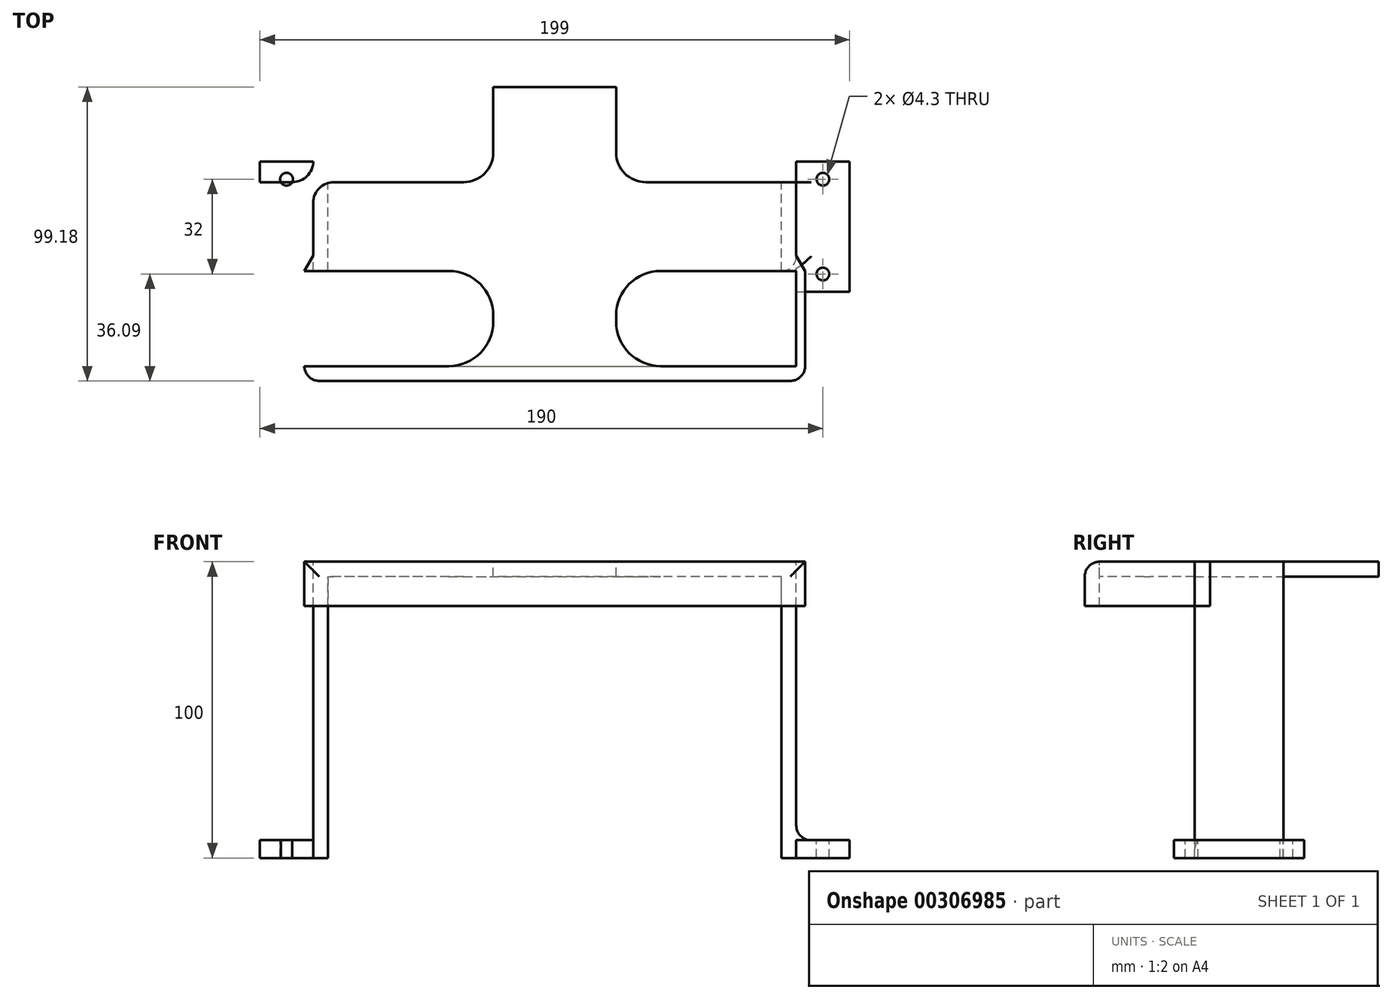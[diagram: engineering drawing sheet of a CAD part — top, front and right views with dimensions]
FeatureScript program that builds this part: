
annotation { "Feature Type Name" : "Feature", "Feature Type Description" : "" }
export const myFeature = defineFeature(function(context is Context, id is Id, definition is map)
    precondition{}
    {
        {
            var Q0;
            Q0=qCreatedBy(makeId("Front.planeOp"),FACE);
            var sketch = newSketch(context, id + "F0", { "sketchPlane" : qUnion([Q0])});
            skLineSegment(sketch, "E0.bottom", {"start": v(76.5, -47.5) * mm, "end": v(-76.5, -47.5) * mm});
            skLineSegment(sketch, "E0.top", {"start": v(76.5, 47.5) * mm, "end": v(-76.5, 47.5) * mm});
            skLineSegment(sketch, "E0.left", {"start": v(76.5, -47.5) * mm, "end": v(76.5, 47.5) * mm});
            skLineSegment(sketch, "E0.right", {"start": v(-76.5, -47.5) * mm, "end": v(-76.5, 47.5) * mm});
            skPoint(sketch, "E0.middle", {"position": v(0, 0) * mm});
            skLineSegment(sketch, "E1", {"start": v(-76.5, -47.5) * mm, "end": v(-99.5, -47.5) * mm});
            skLineSegment(sketch, "E2", {"start": v(-99.5, -47.5) * mm, "end": v(-99.5, -41.5) * mm});
            skLineSegment(sketch, "E3", {"start": v(-99.5, -41.5) * mm, "end": v(99.5, -41.5) * mm});
            skLineSegment(sketch, "E4", {"start": v(99.5, -41.5) * mm, "end": v(99.5, -47.5) * mm});
            skLineSegment(sketch, "E5", {"start": v(99.5, -47.5) * mm, "end": v(76.5, -47.5) * mm});
            skLineSegment(sketch, "E6.bottom", {"start": v(-81.5, -41.5) * mm, "end": v(81.5, -41.5) * mm});
            skLineSegment(sketch, "E6.top", {"start": v(-81.5, 52.5) * mm, "end": v(81.5, 52.5) * mm});
            skLineSegment(sketch, "E6.left", {"start": v(-81.5, -41.5) * mm, "end": v(-81.5, 52.5) * mm});
            skLineSegment(sketch, "E6.right", {"start": v(81.5, -41.5) * mm, "end": v(81.5, 52.5) * mm});
            skSolve(sketch);
        }
        {
            var Q0;
            {var subQ5=sQuery(id+"F0.wireOp",EDGE,"E0.top");Q0=makeQuery(id+"F0.imprint","IMPRINT",FACE,{"disambiguationData":[TD([[makeQuery(id+"F0.imprint","IMPRINT",EDGE,{"derivedFrom":subQ5}),-1.0]])]});}
            var Q1;
            {var subQ4=sQuery(id+"F0.wireOp",EDGE,"E1");Q1=makeQuery(id+"F0.imprint","IMPRINT",FACE,{"disambiguationData":[TD([[makeQuery(id+"F0.imprint","IMPRINT",EDGE,{"derivedFrom":subQ4}),-1.0]])]});}
            var Q2;
            {var subQ1=sQuery(id+"F0.wireOp",EDGE,"E4");Q2=makeQuery(id+"F0.imprint","IMPRINT",FACE,{"disambiguationData":[TD([[makeQuery(id+"F0.imprint","IMPRINT",EDGE,{"derivedFrom":subQ1}),-1.0]])]});}
            extrude(context, id + "F1", {"entities" : qUnion([Q0, Q1, Q2]), "depth" : 30 * mm});
        }
        {
            var Q0;
            {var subQ0=sQuery(id+"F0.wireOp",EDGE,"E3");Q0=makeQuery(id+"F1.opExtrude","SWEPT_FACE",FACE,{"disambiguationData":[OSD([subQ0]),TDD([makeQuery(id+"F0.imprint","IMPRINT",EDGE,{"disambiguationData":[TD([[makeQuery(id+"F0.imprint","INTERSECT",VERTEX,{"derivedFrom":[subQ0,sQuery(id+"F0.wireOp",EDGE,"E4")]}),1.0]])],"derivedFrom":subQ0})])]});}
            var sketch = newSketch(context, id + "F2", { "sketchPlane" : qUnion([Q0])});
            skLineSegment(sketch, "E7", {"start": v(90.5, 0) * mm, "end": v(90.5, -30) * mm, "construction": true});
            skLineSegment(sketch, "E8", {"start": v(81.5, 1) * mm, "end": v(99.5, 1) * mm, "construction": true});
            skLineSegment(sketch, "E9", {"start": v(99.5, -31) * mm, "end": v(81.5, -31) * mm, "construction": true});
            skCircle(sketch, "E10", {"center": v(90.5, 1) * mm, "radius": 2.15 * mm});
            skCircle(sketch, "E11", {"center": v(90.5, -31) * mm, "radius": 2.15 * mm});
            skLineSegment(sketch, "E12", {"start": v(-81.5, 0) * mm, "end": v(-99.5, 0) * mm, "construction": true});
            skLineSegment(sketch, "E13.bottom", {"start": v(-99.5, 0) * mm, "end": v(-81.5, 0) * mm});
            skLineSegment(sketch, "E13.top", {"start": v(-99.5, -30) * mm, "end": v(-81.5, -30) * mm, "construction": true});
            skLineSegment(sketch, "E13.left", {"start": v(-99.5, 0) * mm, "end": v(-99.5, -30) * mm, "construction": true});
            skLineSegment(sketch, "E13.right", {"start": v(-81.5, 0) * mm, "end": v(-81.5, -30) * mm, "construction": true});
            skLineSegment(sketch, "E14", {"start": v(-99.5, 1) * mm, "end": v(-81.5, 1) * mm, "construction": true});
            skLineSegment(sketch, "E15", {"start": v(-81.5, 1) * mm, "end": v(-81.5, -31) * mm, "construction": true});
            skLineSegment(sketch, "E16", {"start": v(-81.5, -31) * mm, "end": v(-99.5, -31) * mm, "construction": true});
            skCircle(sketch, "E17", {"center": v(-90.5, 1) * mm, "radius": 2.15 * mm});
            skCircle(sketch, "E18", {"center": v(-90.5, -31) * mm, "radius": 2.15 * mm});
            skLineSegment(sketch, "E19.bottom", {"start": v(81.5, -37) * mm, "end": v(99.5, -37) * mm});
            skLineSegment(sketch, "E19.top", {"start": v(81.5, 7) * mm, "end": v(99.5, 7) * mm});
            skLineSegment(sketch, "E19.left", {"start": v(81.5, -37) * mm, "end": v(81.5, 7) * mm});
            skLineSegment(sketch, "E19.right", {"start": v(99.5, -37) * mm, "end": v(99.5, 7) * mm});
            skLineSegment(sketch, "E20.bottom", {"start": v(-99.5, -37) * mm, "end": v(-81.5, -37) * mm});
            skLineSegment(sketch, "E20.top", {"start": v(-99.5, 7) * mm, "end": v(-81.5, 7) * mm});
            skLineSegment(sketch, "E20.left", {"start": v(-99.5, -37) * mm, "end": v(-99.5, 7) * mm});
            skLineSegment(sketch, "E20.right", {"start": v(-81.5, -37) * mm, "end": v(-81.5, 7) * mm});
            skSolve(sketch);
        }
        {
            var Q0;
            Q0=makeQuery(id+"F1.opExtrude","SWEPT_FACE",FACE,{"disambiguationData":[OSD([sQuery(id+"F0.wireOp",EDGE,"E6.top")])]});
            var sketch = newSketch(context, id + "F3", { "sketchPlane" : qUnion([Q0])});
            skLineSegment(sketch, "E21.bottom", {"start": v(30.72, 0) * mm, "end": v(81.5, 0) * mm});
            skLineSegment(sketch, "E21.top", {"start": v(-81.5, -30) * mm, "end": v(-35.72, -30) * mm});
            skLineSegment(sketch, "E21.left", {"start": v(-81.5, 0) * mm, "end": v(-81.5, -30) * mm});
            skLineSegment(sketch, "E21.right", {"start": v(81.5, 0) * mm, "end": v(81.5, -30) * mm});
            skLineSegment(sketch, "E22", {"start": v(0, 0) * mm, "end": v(0, -30) * mm, "construction": true});
            skLineSegment(sketch, "E23.top", {"start": v(20.72, 32.1) * mm, "end": v(-20.72, 32.1) * mm});
            skLineSegment(sketch, "E23.left", {"start": v(20.72, -47.09) * mm, "end": v(20.72, -45) * mm});
            skLineSegment(sketch, "E23.right", {"start": v(-20.72, -47.1) * mm, "end": v(-20.72, -45) * mm});
            skPoint(sketch, "E23.middle", {"position": v(0, -15) * mm});
            skLineSegment(sketch, "E24.bottom", {"start": v(-81.5, -62.09) * mm, "end": v(-35.72, -62.09) * mm});
            skLineSegment(sketch, "E24.top", {"start": v(-81.5, -67.1) * mm, "end": v(81.5, -67.1) * mm});
            skLineSegment(sketch, "E24.left", {"start": v(-81.5, -62.09) * mm, "end": v(-81.5, -67.1) * mm});
            skLineSegment(sketch, "E24.right", {"start": v(81.5, -62.09) * mm, "end": v(81.5, -67.09) * mm});
            skLineSegment(sketch, "E25.bottom", {"start": v(81.5, -62.09) * mm, "end": v(84.5, -62.09) * mm});
            skLineSegment(sketch, "E25.top", {"start": v(81.5, -67.1) * mm, "end": v(84.5, -67.1) * mm});
            skLineSegment(sketch, "E25.left", {"start": v(81.5, -62.09) * mm, "end": v(81.5, -67.1) * mm});
            skLineSegment(sketch, "E25.right", {"start": v(84.5, -62.09) * mm, "end": v(84.5, -67.09) * mm});
            skLineSegment(sketch, "E26.bottom", {"start": v(-81.5, -67.1) * mm, "end": v(-84.5, -67.1) * mm});
            skLineSegment(sketch, "E26.top", {"start": v(-81.5, -62.09) * mm, "end": v(-84.5, -62.09) * mm});
            skLineSegment(sketch, "E26.left", {"start": v(-81.5, -67.1) * mm, "end": v(-81.5, -62.09) * mm});
            skLineSegment(sketch, "E26.right", {"start": v(-84.5, -67.1) * mm, "end": v(-84.5, -62.09) * mm});
            skLineSegment(sketch, "E27.trimOffspring", {"start": v(35.72, -62.09) * mm, "end": v(81.5, -62.09) * mm});
            skPoint(sketch, "E28.visualSharp", {"position": v(20.72, -62.09) * mm});
            skArc(sketch, "E28.filletArc", {"start": v(20.72, -47.1) * mm, "mid": v(25.12, -57.7) * mm, "end": v(35.72, -62.09) * mm});
            skPoint(sketch, "E29.visualSharp", {"position": v(-20.72, -62.09) * mm});
            skArc(sketch, "E29.filletArc", {"start": v(-35.72, -62.1) * mm, "mid": v(-25.12, -57.7) * mm, "end": v(-20.72, -47.1) * mm});
            skLineSegment(sketch, "E30", {"start": v(20.72, 10) * mm, "end": v(20.72, 32.1) * mm});
            skLineSegment(sketch, "E31", {"start": v(35.72, -30) * mm, "end": v(81.5, -30) * mm});
            skArc(sketch, "E32.filletArc", {"start": v(-20.72, -45) * mm, "mid": v(-25.12, -34.4) * mm, "end": v(-35.72, -30) * mm});
            skArc(sketch, "E33.filletArc", {"start": v(35.72, -30) * mm, "mid": v(25.12, -34.4) * mm, "end": v(20.72, -45) * mm});
            skLineSegment(sketch, "E34", {"start": v(-20.72, 32.1) * mm, "end": v(-20.72, 10) * mm});
            skLineSegment(sketch, "E35.bottom", {"start": v(-20.72, 32.1) * mm, "end": v(20.72, 32.1) * mm});
            skLineSegment(sketch, "E35.top", {"start": v(-20.72, 37.09) * mm, "end": v(20.72, 37.09) * mm});
            skLineSegment(sketch, "E35.left", {"start": v(-20.72, 32.1) * mm, "end": v(-20.72, 37.09) * mm});
            skLineSegment(sketch, "E35.right", {"start": v(20.72, 32.1) * mm, "end": v(20.72, 37.09) * mm});
            skArc(sketch, "E36.filletArc", {"start": v(20.72, 10) * mm, "mid": v(23.65, 2.93) * mm, "end": v(30.72, 0) * mm});
            skLineSegment(sketch, "E37", {"start": v(-30.72, 0) * mm, "end": v(-32.78, 0) * mm});
            skPoint(sketch, "E38.visualSharp", {"position": v(-20.72, 0) * mm});
            skArc(sketch, "E38.filletArc", {"start": v(-30.72, 0) * mm, "mid": v(-23.65, 2.93) * mm, "end": v(-20.72, 10) * mm});
            skLineSegment(sketch, "E39", {"start": v(-81.5, -62.09) * mm, "end": v(81.5, -62.09) * mm});
            skLineSegment(sketch, "E40", {"start": v(30.72, 0) * mm, "end": v(-30.72, 0) * mm});
            skLineSegment(sketch, "E41.bottom", {"start": v(-84.5, -62.09) * mm, "end": v(-81.5, -62.09) * mm});
            skLineSegment(sketch, "E41.top", {"start": v(-84.5, -30) * mm, "end": v(-81.5, -30) * mm});
            skLineSegment(sketch, "E41.left", {"start": v(-84.5, -62.09) * mm, "end": v(-84.5, -30) * mm});
            skLineSegment(sketch, "E41.right", {"start": v(-81.5, -62.09) * mm, "end": v(-81.5, -30) * mm});
            skLineSegment(sketch, "E42.top", {"start": v(81.5, -30) * mm, "end": v(84.5, -30) * mm});
            skLineSegment(sketch, "E42.left", {"start": v(81.5, -62.09) * mm, "end": v(81.5, -30) * mm});
            skLineSegment(sketch, "E42.right", {"start": v(84.5, -62.09) * mm, "end": v(84.5, -30) * mm});
            skLineSegment(sketch, "E43", {"start": v(-84.5, -30) * mm, "end": v(-81.5, -24.8) * mm});
            skLineSegment(sketch, "E44", {"start": v(84.5, -30) * mm, "end": v(81.5, -24.8) * mm});
            skSolve(sketch);
        }
        {
            var Q0;
            Q0=makeQuery(id+"F3.imprint","IMPRINT",FACE,{"disambiguationData":[TD([[makeQuery(id+"F3.imprint","IMPRINT",EDGE,{"derivedFrom":sQuery(id+"F3.wireOp",EDGE,"E30")}),1.0]])]});
            var Q1;
            Q1=makeQuery(id+"F3.imprint","IMPRINT",FACE,{"disambiguationData":[TD([[makeQuery(id+"F3.imprint","IMPRINT",EDGE,{"derivedFrom":sQuery(id+"F3.wireOp",EDGE,"E23.left")}),1.0]])]});
            extrude(context, id + "F4", {"entities" : qUnion([Q0, Q1]), "operationType" : NewBodyOperationType.ADD, "oppositeDirection" : true, "depth" : 5 * mm});
        }
        {
            var Q0;
            Q0=makeQuery(id+"F3.imprint","IMPRINT",FACE,{"disambiguationData":[TD([[makeQuery(id+"F3.imprint","IMPRINT",EDGE,{"derivedFrom":sQuery(id+"F3.wireOp",EDGE,"E41.bottom")}),1.0]])]});
            var Q1;
            Q1=makeQuery(id+"F3.imprint","IMPRINT",FACE,{"disambiguationData":[TD([[makeQuery(id+"F3.imprint","IMPRINT",EDGE,{"derivedFrom":sQuery(id+"F3.wireOp",EDGE,"E24.top")}),1.0]])]});
            var Q2;
            Q2=makeQuery(id+"F3.imprint","IMPRINT",FACE,{"disambiguationData":[TD([[makeQuery(id+"F3.imprint","IMPRINT",EDGE,{"derivedFrom":sQuery(id+"F3.wireOp",EDGE,"E26.bottom")}),-1.0]])]});
            var Q3;
            Q3=makeQuery(id+"F3.imprint","IMPRINT",FACE,{"disambiguationData":[TD([[makeQuery(id+"F3.imprint","IMPRINT",EDGE,{"derivedFrom":sQuery(id+"F3.wireOp",EDGE,"E25.bottom")}),1.0]])]});
            var Q4;
            Q4=makeQuery(id+"F3.imprint","IMPRINT",FACE,{"disambiguationData":[TD([[makeQuery(id+"F3.imprint","IMPRINT",EDGE,{"derivedFrom":sQuery(id+"F3.wireOp",EDGE,"E25.top")}),1.0]])]});
            var Q5;
            {var subQ0=sQuery(id+"F3.wireOp",EDGE,"E42.top");Q5=makeQuery(id+"F3.imprint","IMPRINT",FACE,{"disambiguationData":[TD([[makeQuery(id+"F3.imprint","IMPRINT",EDGE,{"derivedFrom":subQ0}),1.0]])]});}
            var Q6;
            {var subQ0=sQuery(id+"F3.wireOp",EDGE,"E41.top");Q6=makeQuery(id+"F3.imprint","IMPRINT",FACE,{"disambiguationData":[TD([[makeQuery(id+"F3.imprint","IMPRINT",EDGE,{"derivedFrom":subQ0}),1.0]])]});}
            var Q7;
            Q7=makeQuery(id+"F3.imprint","IMPRINT",FACE,{"disambiguationData":[TD([[makeQuery(id+"F3.imprint","IMPRINT",EDGE,{"derivedFrom":sQuery(id+"F3.wireOp",EDGE,"E35.bottom")}),1.0]])]});
            extrude(context, id + "F5", {"entities" : qUnion([Q0, Q1, Q2, Q3, Q4, Q5, Q6, Q7]), "operationType" : NewBodyOperationType.ADD, "oppositeDirection" : true, "depth" : 15 * mm});
        }
        {
            var Q0;
            Q0=makeQuery(id+"F5.opExtrude","SWEPT_EDGE",EDGE,{"disambiguationData":[OSD([sQuery(id+"F3.wireOp",EDGE,"E25.top"),sQuery(id+"F3.wireOp",EDGE,"E25.right")])]});
            var Q1;
            Q1=makeQuery(id+"F5.opExtrude","SWEPT_EDGE",EDGE,{"disambiguationData":[OSD([sQuery(id+"F3.wireOp",EDGE,"E26.bottom"),sQuery(id+"F3.wireOp",EDGE,"E26.right")])]});
            var Q2;
            Q2=makeQuery(id+"F5.opExtrude","CAP_EDGE",EDGE,{"disambiguationData":[OSD([sQuery(id+"F3.wireOp",EDGE,"E24.top"),sQuery(id+"F3.wireOp",EDGE,"E25.top"),sQuery(id+"F3.wireOp",EDGE,"E26.bottom")])],"isStart":true});
            fillet(context, id + "F6", {"entities" : qUnion([Q0, Q1, Q2]), "radius" : 5 * mm, "tangentPropagation" : true, "allowEdgeOverflow" : false});
        }
        {
            var Q0;
            {var subQ4=sQuery(id+"F2.wireOp",EDGE,"E19.top");Q0=makeQuery(id+"F2.imprint","IMPRINT",FACE,{"disambiguationData":[TD([[makeQuery(id+"F2.imprint","IMPRINT",EDGE,{"derivedFrom":subQ4}),-1.0]])]});}
            var Q1;
            {var subQ4=sQuery(id+"F2.wireOp",EDGE,"E19.bottom");Q1=makeQuery(id+"F2.imprint","IMPRINT",FACE,{"disambiguationData":[TD([[makeQuery(id+"F2.imprint","IMPRINT",EDGE,{"derivedFrom":subQ4}),1.0]])]});}
            var Q2;
            Q2=makeQuery(id+"F2.imprint","IMPRINT",FACE,{"disambiguationData":[TD([[makeQuery(id+"F2.imprint","IMPRINT",EDGE,{"derivedFrom":sQuery(id+"F2.wireOp",EDGE,"E18")}),-1.0]])]});
            var Q3;
            {var subQ4=sQuery(id+"F2.wireOp",EDGE,"E20.top");Q3=makeQuery(id+"F2.imprint","IMPRINT",FACE,{"disambiguationData":[TD([[makeQuery(id+"F2.imprint","IMPRINT",EDGE,{"derivedFrom":subQ4}),-1.0]])]});}
            extrude(context, id + "F7", {"entities" : qUnion([Q0, Q1, Q2, Q3]), "operationType" : NewBodyOperationType.ADD, "oppositeDirection" : true, "depth" : 6 * mm});
        }
        {
            var Q0;
            {var subQ0=sQuery(id+"F2.wireOp",EDGE,"E11");var subQ1=sQuery(id+"F0.wireOp",EDGE,"E3");var subQ2=makeQuery(id+"F1.opExtrude","CAP_EDGE",EDGE,{"disambiguationData":[OSD([subQ1]),TDD([makeQuery(id+"F0.imprint","IMPRINT",EDGE,{"disambiguationData":[TD([[makeQuery(id+"F0.imprint","INTERSECT",VERTEX,{"derivedFrom":[subQ1,sQuery(id+"F0.wireOp",EDGE,"E4")]}),1.0]])],"derivedFrom":subQ1})])],"isStart":false});var subQ3=makeQuery(id+"F2.imprint","INTERSECT",VERTEX,{"disambiguationData":[OD(0.0)],"derivedFrom":[subQ2,subQ0]});Q0=makeQuery(id+"F2.imprint","IMPRINT",FACE,{"disambiguationData":[TD([[makeQuery(id+"F2.imprint","IMPRINT",EDGE,{"disambiguationData":[TD([[subQ3,-1.0]])],"derivedFrom":subQ0}),1.0]])]});}
            var Q1;
            {var subQ0=sQuery(id+"F2.wireOp",EDGE,"E10");var subQ1=sQuery(id+"F0.wireOp",EDGE,"E3");var subQ2=makeQuery(id+"F1.opExtrude","CAP_EDGE",EDGE,{"disambiguationData":[OSD([subQ1]),TDD([makeQuery(id+"F0.imprint","IMPRINT",EDGE,{"disambiguationData":[TD([[makeQuery(id+"F0.imprint","INTERSECT",VERTEX,{"derivedFrom":[subQ1,sQuery(id+"F0.wireOp",EDGE,"E4")]}),1.0]])],"derivedFrom":subQ1})])],"isStart":true});var subQ3=makeQuery(id+"F2.imprint","INTERSECT",VERTEX,{"disambiguationData":[OD(0.0)],"derivedFrom":[subQ2,subQ0]});Q1=makeQuery(id+"F2.imprint","IMPRINT",FACE,{"disambiguationData":[TD([[makeQuery(id+"F2.imprint","IMPRINT",EDGE,{"disambiguationData":[TD([[subQ3,1.0]])],"derivedFrom":subQ0}),1.0]])]});}
            var Q2;
            Q2=makeQuery(id+"F2.imprint","IMPRINT",FACE,{"disambiguationData":[TD([[makeQuery(id+"F2.imprint","IMPRINT",EDGE,{"derivedFrom":sQuery(id+"F2.wireOp",EDGE,"E18")}),1.0]])]});
            var Q3;
            {var subQ0=sQuery(id+"F2.wireOp",EDGE,"E17");var subQ1=sQuery(id+"F2.wireOp",EDGE,"E13.bottom");var subQ2=makeQuery(id+"F2.imprint","INTERSECT",VERTEX,{"disambiguationData":[OD(0.0)],"derivedFrom":[subQ1,subQ0]});Q3=makeQuery(id+"F2.imprint","IMPRINT",FACE,{"disambiguationData":[TD([[makeQuery(id+"F2.imprint","IMPRINT",EDGE,{"disambiguationData":[TD([[subQ2,-1.0]])],"derivedFrom":subQ1}),-1.0]])]});}
            extrude(context, id + "F8", {"entities" : qUnion([Q0, Q1, Q2, Q3]), "operationType" : NewBodyOperationType.REMOVE, "oppositeDirection" : true, "depth" : 25 * mm});
        }
        {
            var Q0;
            {var subQ0=sQuery(id+"F2.wireOp",EDGE,"E19.left");var subQ1=sQuery(id+"F0.wireOp",EDGE,"E3");Q0=makeQuery(id+"F7.opExtrude","SWEPT_EDGE",EDGE,{"disambiguationData":[OSD([subQ1,subQ0]),TDD([makeQuery(id+"F2.imprint","INTERSECT",VERTEX,{"derivedFrom":[makeQuery(id+"F1.opExtrude","CAP_EDGE",EDGE,{"disambiguationData":[OSD([subQ1]),TDD([makeQuery(id+"F0.imprint","IMPRINT",EDGE,{"disambiguationData":[TD([[makeQuery(id+"F0.imprint","INTERSECT",VERTEX,{"derivedFrom":[subQ1,sQuery(id+"F0.wireOp",EDGE,"E4")]}),1.0]])],"derivedFrom":subQ1})])],"isStart":false}),subQ0]})])]});}
            var Q1;
            {var subQ0=sQuery(id+"F2.wireOp",EDGE,"E19.left");var subQ1=sQuery(id+"F0.wireOp",EDGE,"E3");Q1=makeQuery(id+"F7.opExtrude","SWEPT_EDGE",EDGE,{"disambiguationData":[OSD([subQ1,subQ0]),TDD([makeQuery(id+"F2.imprint","INTERSECT",VERTEX,{"derivedFrom":[makeQuery(id+"F1.opExtrude","CAP_EDGE",EDGE,{"disambiguationData":[OSD([subQ1]),TDD([makeQuery(id+"F0.imprint","IMPRINT",EDGE,{"disambiguationData":[TD([[makeQuery(id+"F0.imprint","INTERSECT",VERTEX,{"derivedFrom":[subQ1,sQuery(id+"F0.wireOp",EDGE,"E4")]}),1.0]])],"derivedFrom":subQ1})])],"isStart":true}),subQ0]})])]});}
            var Q2;
            {var subQ7=sQuery(id+"F0.wireOp",EDGE,"E6.top");var subQ8=sQuery(id+"F0.wireOp",EDGE,"E0.top");var subQ9=sQuery(id+"F0.wireOp",EDGE,"E6.left");var subQ10=sQuery(id+"F0.wireOp",EDGE,"E3");var subQ11=sQuery(id+"F0.wireOp",EDGE,"E2");var subQ18=sQuery(id+"F0.wireOp",EDGE,"E1");var subQ19=sQuery(id+"F0.wireOp",EDGE,"E0.right");Q2=makeQuery(id+"F7.boolean.opBoolean","INTERSECT",EDGE,{"derivedFrom":[makeQuery(id+"F4.boolean.opBoolean","SPLIT",FACE,{"disambiguationData":[TD([makeQuery(id+"F1.opExtrude","SWEPT_FACE",FACE,{"disambiguationData":[OSD([subQ19])]})])],"derivedFrom":makeQuery(id+"F1.opExtrude","CAP_FACE",FACE,{"disambiguationData":[OSD([subQ8,sQuery(id+"F0.wireOp",EDGE,"E0.left"),subQ19,subQ18,subQ11,subQ10,sQuery(id+"F0.wireOp",EDGE,"E4"),sQuery(id+"F0.wireOp",EDGE,"E5"),subQ7,subQ9,sQuery(id+"F0.wireOp",EDGE,"E6.right")])],"isStart":true})}),makeQuery(id+"F7.opExtrude","SWEPT_FACE",FACE,{"disambiguationData":[OSD([sQuery(id+"F2.wireOp",EDGE,"E20.right")])]})]});}
            var Q3;
            {var subQ7=sQuery(id+"F0.wireOp",EDGE,"E6.top");var subQ8=sQuery(id+"F0.wireOp",EDGE,"E0.top");var subQ9=sQuery(id+"F0.wireOp",EDGE,"E6.left");var subQ10=sQuery(id+"F0.wireOp",EDGE,"E3");var subQ11=sQuery(id+"F0.wireOp",EDGE,"E2");var subQ18=sQuery(id+"F0.wireOp",EDGE,"E1");var subQ19=sQuery(id+"F0.wireOp",EDGE,"E0.right");Q3=makeQuery(id+"F7.boolean.opBoolean","INTERSECT",EDGE,{"derivedFrom":[makeQuery(id+"F4.boolean.opBoolean","SPLIT",FACE,{"disambiguationData":[TD([makeQuery(id+"F1.opExtrude","SWEPT_FACE",FACE,{"disambiguationData":[OSD([subQ19])]})])],"derivedFrom":makeQuery(id+"F1.opExtrude","CAP_FACE",FACE,{"disambiguationData":[OSD([subQ8,sQuery(id+"F0.wireOp",EDGE,"E0.left"),subQ19,subQ18,subQ11,subQ10,sQuery(id+"F0.wireOp",EDGE,"E4"),sQuery(id+"F0.wireOp",EDGE,"E5"),subQ7,subQ9,sQuery(id+"F0.wireOp",EDGE,"E6.right")])],"isStart":false})}),makeQuery(id+"F7.opExtrude","SWEPT_FACE",FACE,{"disambiguationData":[OSD([sQuery(id+"F2.wireOp",EDGE,"E20.right")])]})]});}
            fillet(context, id + "F9", {"entities" : qUnion([Q0, Q1, Q2, Q3]), "radius" : 7 * mm, "tangentPropagation" : true, "allowEdgeOverflow" : false});
        }
        {
            var Q0;
            Q0=makeQuery(id+"F9.opFillet","TWEAK_EDGE",EDGE,{"derivedFrom":[makeQuery(id+"F1.opExtrude","CAP_VERTEX",VERTEX,{"disambiguationData":[OSD([sQuery(id+"F0.wireOp",EDGE,"E3"),sQuery(id+"F0.wireOp",EDGE,"E6.bottom"),sQuery(id+"F0.wireOp",EDGE,"E6.left")])],"isStart":false})]});
            var Q1;
            Q1=makeQuery(id+"F9.opFillet","TWEAK_EDGE",EDGE,{"derivedFrom":[makeQuery(id+"F1.opExtrude","CAP_VERTEX",VERTEX,{"disambiguationData":[OSD([sQuery(id+"F0.wireOp",EDGE,"E3"),sQuery(id+"F0.wireOp",EDGE,"E6.bottom"),sQuery(id+"F0.wireOp",EDGE,"E6.left")])],"isStart":true})]});
            var Q2;
            {var subQ0=sQuery(id+"F2.wireOp",EDGE,"E19.left");var subQ1=sQuery(id+"F0.wireOp",EDGE,"E3");var subQ2=sQuery(id+"F0.wireOp",EDGE,"E6.right");var subQ3=sQuery(id+"F0.wireOp",EDGE,"E6.bottom");Q2=makeQuery(id+"F9.opFillet","TWEAK_EDGE",EDGE,{"derivedFrom":[makeQuery(id+"F7.boolean.opBoolean","MERGE",VERTEX,{"derivedFrom":[makeQuery(id+"F1.opExtrude","CAP_VERTEX",VERTEX,{"disambiguationData":[OSD([subQ1,subQ3,subQ2])],"isStart":true}),makeQuery(id+"F7.opExtrude","CAP_VERTEX",VERTEX,{"disambiguationData":[OSD([subQ1,subQ0]),TDD([makeQuery(id+"F2.imprint","INTERSECT",VERTEX,{"derivedFrom":[makeQuery(id+"F1.opExtrude","CAP_EDGE",EDGE,{"disambiguationData":[OSD([subQ1]),TDD([makeQuery(id+"F0.imprint","IMPRINT",EDGE,{"disambiguationData":[TD([[makeQuery(id+"F0.imprint","INTERSECT",VERTEX,{"derivedFrom":[subQ1,sQuery(id+"F0.wireOp",EDGE,"E4")]}),1.0]])],"derivedFrom":subQ1})])],"isStart":true}),subQ0]})])],"isStart":true})]})]});}
            var Q3;
            {var subQ0=sQuery(id+"F2.wireOp",EDGE,"E19.left");var subQ1=sQuery(id+"F0.wireOp",EDGE,"E3");var subQ2=sQuery(id+"F0.wireOp",EDGE,"E6.right");var subQ3=sQuery(id+"F0.wireOp",EDGE,"E6.bottom");Q3=makeQuery(id+"F9.opFillet","TWEAK_EDGE",EDGE,{"derivedFrom":[makeQuery(id+"F7.boolean.opBoolean","MERGE",VERTEX,{"derivedFrom":[makeQuery(id+"F1.opExtrude","CAP_VERTEX",VERTEX,{"disambiguationData":[OSD([subQ1,subQ3,subQ2])],"isStart":false}),makeQuery(id+"F7.opExtrude","CAP_VERTEX",VERTEX,{"disambiguationData":[OSD([subQ1,subQ0]),TDD([makeQuery(id+"F2.imprint","INTERSECT",VERTEX,{"derivedFrom":[makeQuery(id+"F1.opExtrude","CAP_EDGE",EDGE,{"disambiguationData":[OSD([subQ1]),TDD([makeQuery(id+"F0.imprint","IMPRINT",EDGE,{"disambiguationData":[TD([[makeQuery(id+"F0.imprint","INTERSECT",VERTEX,{"derivedFrom":[subQ1,sQuery(id+"F0.wireOp",EDGE,"E4")]}),1.0]])],"derivedFrom":subQ1})])],"isStart":false}),subQ0]})])],"isStart":true})]})]});}
            var Q4;
            Q4=makeQuery(id+"F1.opExtrude","SWEPT_EDGE",EDGE,{"disambiguationData":[OSD([sQuery(id+"F0.wireOp",EDGE,"E3"),sQuery(id+"F0.wireOp",EDGE,"E6.bottom"),sQuery(id+"F0.wireOp",EDGE,"E6.right")])]});
            var Q5;
            Q5=makeQuery(id+"F1.opExtrude","SWEPT_EDGE",EDGE,{"disambiguationData":[OSD([sQuery(id+"F0.wireOp",EDGE,"E3"),sQuery(id+"F0.wireOp",EDGE,"E6.bottom"),sQuery(id+"F0.wireOp",EDGE,"E6.left")])]});
            fillet(context, id + "F10", {"entities" : qUnion([Q0, Q1, Q2, Q3, Q4, Q5]), "radius" : 5 * mm, "tangentPropagation" : true, "allowEdgeOverflow" : false});
        }
        {
            var Q0;
            {var subQ0=sQuery(id+"F0.wireOp",EDGE,"E6.left");Q0=makeQuery(id+"F5.boolean.opBoolean","SPLIT",EDGE,{"disambiguationData":[topologyDisambiguationEdgeConnected([makeQuery(id+"F5.opExtrude","SWEPT_FACE",FACE,{"disambiguationData":[OSD([sQuery(id+"F3.wireOp",EDGE,"E21.left"),sQuery(id+"F3.wireOp",EDGE,"E41.right")])]})])],"derivedFrom":makeQuery(id+"F1.opExtrude","CAP_EDGE",EDGE,{"disambiguationData":[OSD([subQ0])],"isStart":false})});}
            var Q1;
            {var subQ0=sQuery(id+"F0.wireOp",EDGE,"E6.right");Q1=makeQuery(id+"F5.boolean.opBoolean","SPLIT",EDGE,{"disambiguationData":[topologyDisambiguationEdgeConnected([makeQuery(id+"F5.opExtrude","SWEPT_FACE",FACE,{"disambiguationData":[OSD([sQuery(id+"F3.wireOp",EDGE,"E21.right"),sQuery(id+"F3.wireOp",EDGE,"E42.left")])]})])],"derivedFrom":makeQuery(id+"F1.opExtrude","CAP_EDGE",EDGE,{"disambiguationData":[OSD([subQ0])],"isStart":false})});}
            fillet(context, id + "F11", {"entities" : qUnion([Q0, Q1]), "radius" : 5 * mm, "tangentPropagation" : true, "allowEdgeOverflow" : false});
        }
    });
